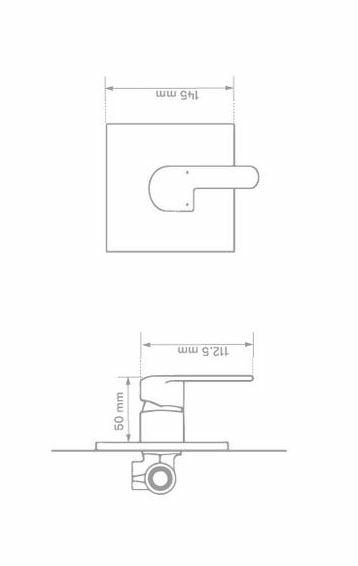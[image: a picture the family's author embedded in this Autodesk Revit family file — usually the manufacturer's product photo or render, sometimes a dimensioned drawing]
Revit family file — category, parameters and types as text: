
# Revit family: 01-1558-11-LLAVE MÓVIL PARED S CUERPO PLÁSTICO PIANA
name_source: partatom
category: Plumbing Fixtures
revit_build: Autodesk Revit 2018 (Build: 20170223_1515(x64)
units: mm (PartAtom-declared; Revit-internal decimal feet)

## family parameters
Cut with Voids When Loaded = No
Host = Face
OmniClass Number = 23.31.11.00
Part Type = Normal
Room Calculation Point = No
Round Connector Dimension = Use Diameter
Shared = No

## types (1)
- 01-1558-11
    Alto = 180 mm  [stored 0.590551 ft]
    Ancho = 75 mm
    CW Connection = Yes
    Default Elevation = 0 mm  [stored 0 ft]
    Description = LLAVE MÓVIL PARED
    Finish = Plastico ABS Cromado
    HW Connection = Yes
    Largo = 260 mm
    Link Ficha Tecnica = http://infotecnica.gricol.com
    Manufacturer = Gricol
    Model = 01-1558-11
    Product Name = LLAVE MÓVIL PARED S CUERPO PLÁSTICO PIANA
    Type Image = LLAVE MOVIL PARED PIANA FOTO.jpg
    URL = https://www.gricol.com
    Vent Connection = No
    Waste Connection = No

note: [stored X ft] marks values corroborated as IEEE doubles in the binary element streams (Revit-internal decimal feet)

## geometry (parser evidence)
native form markers: Blend x2, Sweep x7
no freeform markers — native parametric forms only
